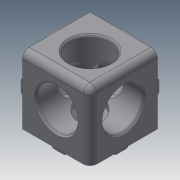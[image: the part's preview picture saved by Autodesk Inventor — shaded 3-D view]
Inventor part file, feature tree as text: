
AUTODESK INVENTOR PART (.ipt)
format: ipt  version: 2018.2 (Build 222227000, 227)  size: 264,192 bytes
history: native  units: in
note: dims shown in document units (in); Inventor stores cm internally (conversion verified against a paired STEP export)
features: mirror x2, revolve x1, chamfer x1
ambient origin geometry x8: Origin, YZ Plane, XZ Plane, XY Plane, X Axis, Y Axis, Z Axis, Center Point
bodies: Solid1 (feature_tree), Solid2 (feature_tree), Solid3 (feature_tree), Solid4 (feature_tree)
feature tree (4):
  revolve  "Revolve1"  [1 undecoded]
  mirror  "Mirror4"
  chamfer  "Chamfer1"  [1 undecoded]
  mirror  "Mirror5"
note: 2 required parameter values undecoded (feature->parameter linkage not recoverable at this tier; creation-order binding heuristic only, values carry confidence <= 0.55)
